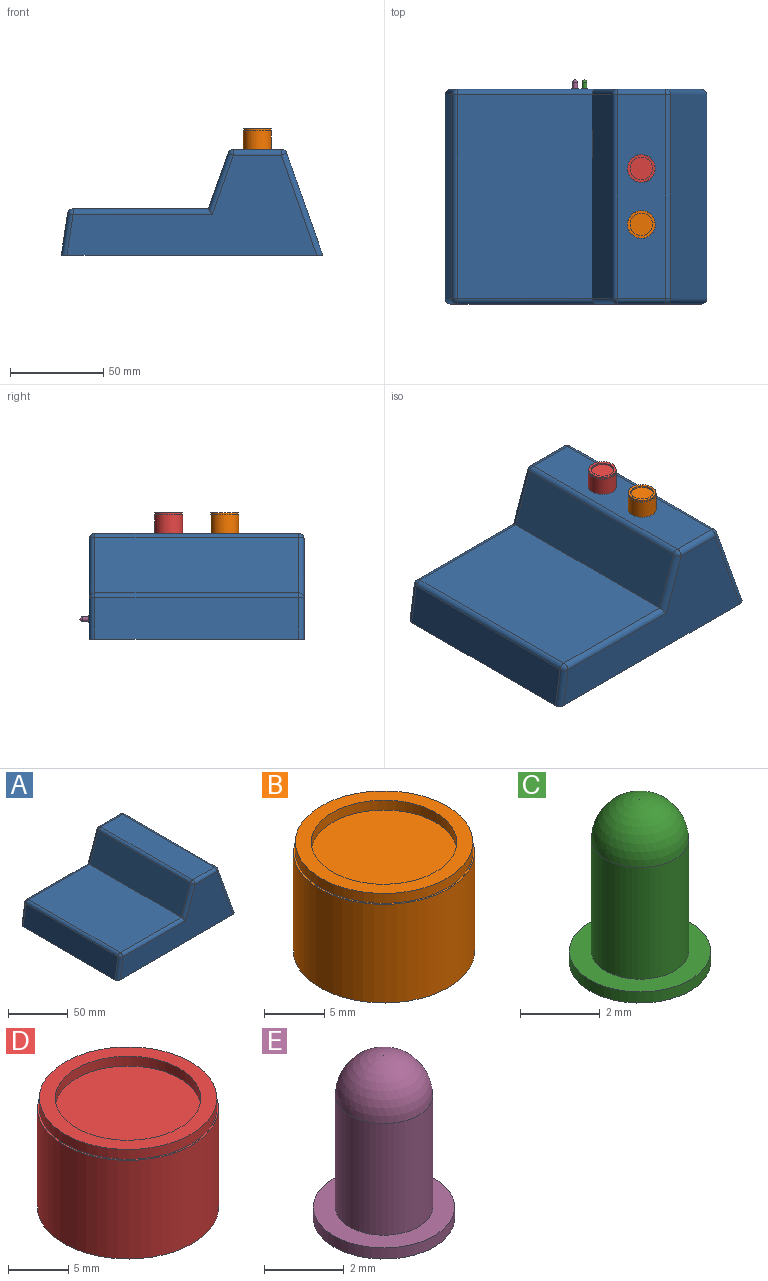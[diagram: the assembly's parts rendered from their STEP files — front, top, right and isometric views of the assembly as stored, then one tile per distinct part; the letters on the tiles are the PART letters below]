
ASSEMBLY  parts=5 mates=4
PART A: 27 faces, bbox 140x115x57.6 mm
  f0: plane 109x54.57mm, normal (0.94,0,0.33), area 6308.8mm2, adj f5,f20,f23,f26
  f1: plane 109x25.76mm, normal (0,0,1), area 2807.6mm2, adj f16,f21,f22,f26
  f2: plane 109x29.85mm, normal (-0.94,0,0.33), area 3451mm2, adj f3,f15,f16,f17
  f3: plane 109x72.42mm, normal (0,0,1), area 7893.7mm2, adj f2,f9,f13,f14
  f4: plane 109x22.17mm, normal (-0.99,0,0.15), area 2443.7mm2, adj f5,f8,f9,f10
  f5: plane 140x115mm, normal (0,0,-1), area 16092mm2, adj f0,f4,f6,f7,f8,f10,f20,f23
  f6: plane 133.78x53.57mm, normal (0,-1,0), area 3965.6mm2, adj f5,f8,f13,f15,f20,f21
  f7: plane 133.78x53.57mm, normal (0,1,0), area 3965.6mm2, adj f5,f10,f14,f17,f22,f23
  f8: cylinder r=3mm len=22.62mm, axis (0.15,0,0.99), area 104.9mm2, adj f4,f5,f6,f11
  f9: cylinder r=3mm len=109mm, axis (0,1,0), area 464.6mm2, adj f3,f4,f11,f12
  f10: cylinder r=3mm len=22.62mm, axis (-0.15,0,-0.99), area 104.9mm2, adj f4,f5,f7,f12
  f11: sphere r=3mm, area 12.8mm2, adj f8,f9,f13
  f12: sphere r=3mm, area 12.8mm2, adj f9,f10,f14
  f13: cylinder r=3mm len=74.54mm, axis (1,0,0), area 344.9mm2, adj f3,f6,f11,f15
  f14: cylinder r=3mm len=74.54mm, axis (-1,0,0), area 344.9mm2, adj f3,f7,f12,f17
  f15: cylinder r=3mm len=32.85mm, axis (0.33,0,0.94), area 152.8mm2, adj f2,f6,f13,f18
  f16: cylinder r=3mm len=109mm, axis (0,-1,0), area 402.5mm2, adj f1,f2,f18,f19
  f17: cylinder r=3mm len=32.85mm, axis (-0.33,0,-0.94), area 152.8mm2, adj f2,f7,f14,f19
  f18: sphere r=3mm, area 11.1mm2, adj f15,f16,f21
  f19: sphere r=3mm, area 11.1mm2, adj f16,f17,f22
  f20: cylinder r=3mm len=55.57mm, axis (0.33,0,-0.94), area 270.9mm2, adj f0,f5,f6,f24
  f21: cylinder r=3mm len=25.76mm, axis (1,0,0), area 121.4mm2, adj f1,f6,f18,f24
  f22: cylinder r=3mm len=25.76mm, axis (-1,0,0), area 121.4mm2, adj f1,f7,f19,f25
  f23: cylinder r=3mm len=55.57mm, axis (-0.33,0,0.94), area 270.9mm2, adj f0,f5,f7,f25
  f24: sphere r=3mm, area 11.1mm2, adj f20,f21,f26
  f25: sphere r=3mm, area 11.1mm2, adj f22,f23,f26
  f26: cylinder r=3mm len=109mm, axis (0,1,0), area 402.5mm2, adj f0,f1,f24,f25
PART B: 7 faces, bbox 15x15x11 mm
  f0: cylinder r=7.5mm len=15mm, axis (0,0,-1), area 471.2mm2, adj f1,f2
  f1: plane 15x15mm, normal (0,0,1), area 7mm2, adj f0,f4
  f2: plane 15x15mm, normal (0,0,-1), area 176.7mm2, adj f0
  f3: cylinder r=6.03mm len=12.06mm, axis (0,0,-1), area 37.9mm2, adj f5,f6
  f4: cylinder r=7.35mm len=14.7mm, axis (0,0,-1), area 46.2mm2, adj f1,f5
  f5: plane 14.7x14.7mm, normal (0,0,1), area 55.5mm2, adj f3,f4
  f6: plane 12.06x12.06mm, normal (0,0,1), area 114.2mm2, adj f3
PART C: 5 faces, bbox 3.6x3.6x5 mm
  f0: cylinder r=1.22mm len=3.44mm, axis (0,0,-1), area 26.4mm2, adj f1,f4
  f1: plane 3.55x3.55mm, normal (0,0,1), area 5.2mm2, adj f0,f2
  f2: cylinder r=1.78mm len=3.55mm, axis (0,0,-1), area 3.8mm2, adj f1,f3
  f3: plane 3.55x3.55mm, normal (0,0,-1), area 9.9mm2, adj f2
  f4: sphere r=1.22mm, area 9.4mm2, adj f0
PART D: 7 faces, bbox 15x15x11 mm
  f0: cylinder r=7.5mm len=15mm, axis (0,0,-1), area 471.2mm2, adj f1,f2
  f1: plane 15x15mm, normal (0,0,1), area 7mm2, adj f0,f4
  f2: plane 15x15mm, normal (0,0,-1), area 176.7mm2, adj f0
  f3: cylinder r=6.03mm len=12.06mm, axis (0,0,-1), area 37.9mm2, adj f5,f6
  f4: cylinder r=7.35mm len=14.7mm, axis (0,0,-1), area 46.2mm2, adj f1,f5
  f5: plane 14.7x14.7mm, normal (0,0,1), area 55.5mm2, adj f3,f4
  f6: plane 12.06x12.06mm, normal (0,0,1), area 114.2mm2, adj f3
PART E: 5 faces, bbox 3.6x3.6x5 mm
  f0: cylinder r=1.22mm len=3.44mm, axis (0,0,-1), area 26.4mm2, adj f1,f4
  f1: plane 3.55x3.55mm, normal (0,0,1), area 5.2mm2, adj f0,f2
  f2: cylinder r=1.78mm len=3.55mm, axis (0,0,-1), area 3.8mm2, adj f1,f3
  f3: plane 3.55x3.55mm, normal (0,0,-1), area 9.9mm2, adj f2
  f4: sphere r=1.22mm, area 9.4mm2, adj f0
PLACE A t=(36.74,83.27,5.51)mm
PLACE B rot(axis=(0,0,-1),90deg) t=(23.95,-11.79,62.08)mm
PLACE C rot(axis=(-1,0,0),90deg) t=(34.99,83.61,16.24)mm
PLACE D t=(94.3,12.98,62.08)mm
PLACE E rot(axis=(-1,0,0),90deg) t=(34.89,83.61,16.24)mm
MATE fastened C.f0 <-> A.f7  axis (0,-1,0) through (21.34,83.27,16.24)mm
MATE fastened E.f0 <-> A.f7  axis (0,-1,0) through (16.34,83.27,16.24)mm
MATE fastened B.f0 <-> A.f1  axis (0,0,-1) through (51.74,10.77,62.08)mm
MATE fastened D.f0 <-> A.f1  axis (0,0,-1) through (51.74,40.77,62.08)mm
